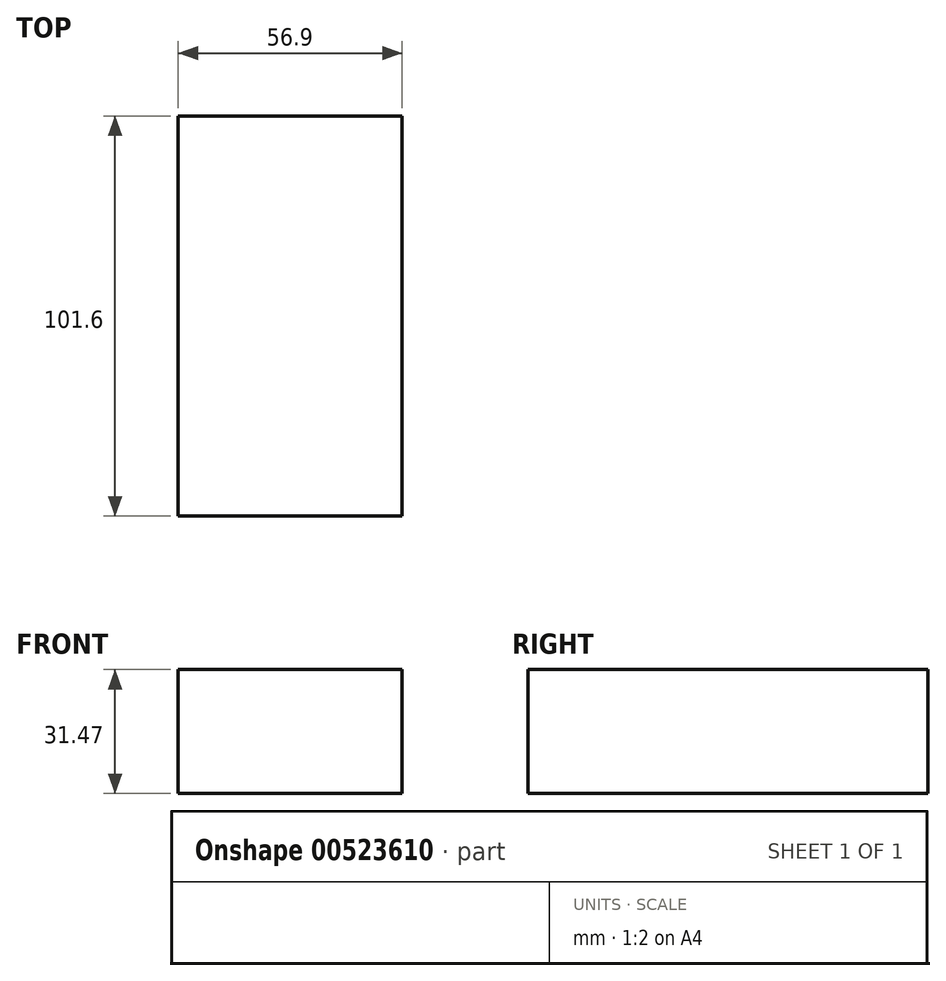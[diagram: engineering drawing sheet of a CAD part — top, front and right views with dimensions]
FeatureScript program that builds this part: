
annotation { "Feature Type Name" : "Feature", "Feature Type Description" : "" }
export const myFeature = defineFeature(function(context is Context, id is Id, definition is map)
    precondition{}
    {
        {
            var Q0;
            Q0=qCreatedBy(makeId("Front.planeOp"),FACE);
            var sketch = newSketch(context, id + "F0", { "sketchPlane" : qUnion([Q0])});
            skLineSegment(sketch, "E0.bottom", {"start": v(-61, 32.98) * mm, "end": v(-4.1, 32.98) * mm});
            skLineSegment(sketch, "E0.top", {"start": v(-61, 1.5) * mm, "end": v(-4.1, 1.5) * mm});
            skLineSegment(sketch, "E0.left", {"start": v(-61, 32.98) * mm, "end": v(-61, 1.5) * mm});
            skLineSegment(sketch, "E0.right", {"start": v(-4.1, 32.98) * mm, "end": v(-4.1, 1.5) * mm});
            skLineSegment(sketch, "E1", {"start": v(-61, 17.24) * mm, "end": v(-41.6, 17.03) * mm});
            skSolve(sketch);
        }
        {
            var Q0;
            {var subQ3=sQuery(id+"F0.wireOp",EDGE,"E0.bottom");Q0=makeQuery(id+"F0.imprint","IMPRINT",FACE,{"disambiguationData":[TD([[makeQuery(id+"F0.imprint","IMPRINT",EDGE,{"derivedFrom":subQ3}),-1.0]])]});}
            extrude(context, id + "F1", {"entities" : qUnion([Q0]), "depth" : 101.6 * mm, "offsetDistance" : 25.4 * mm});
        }
    });
